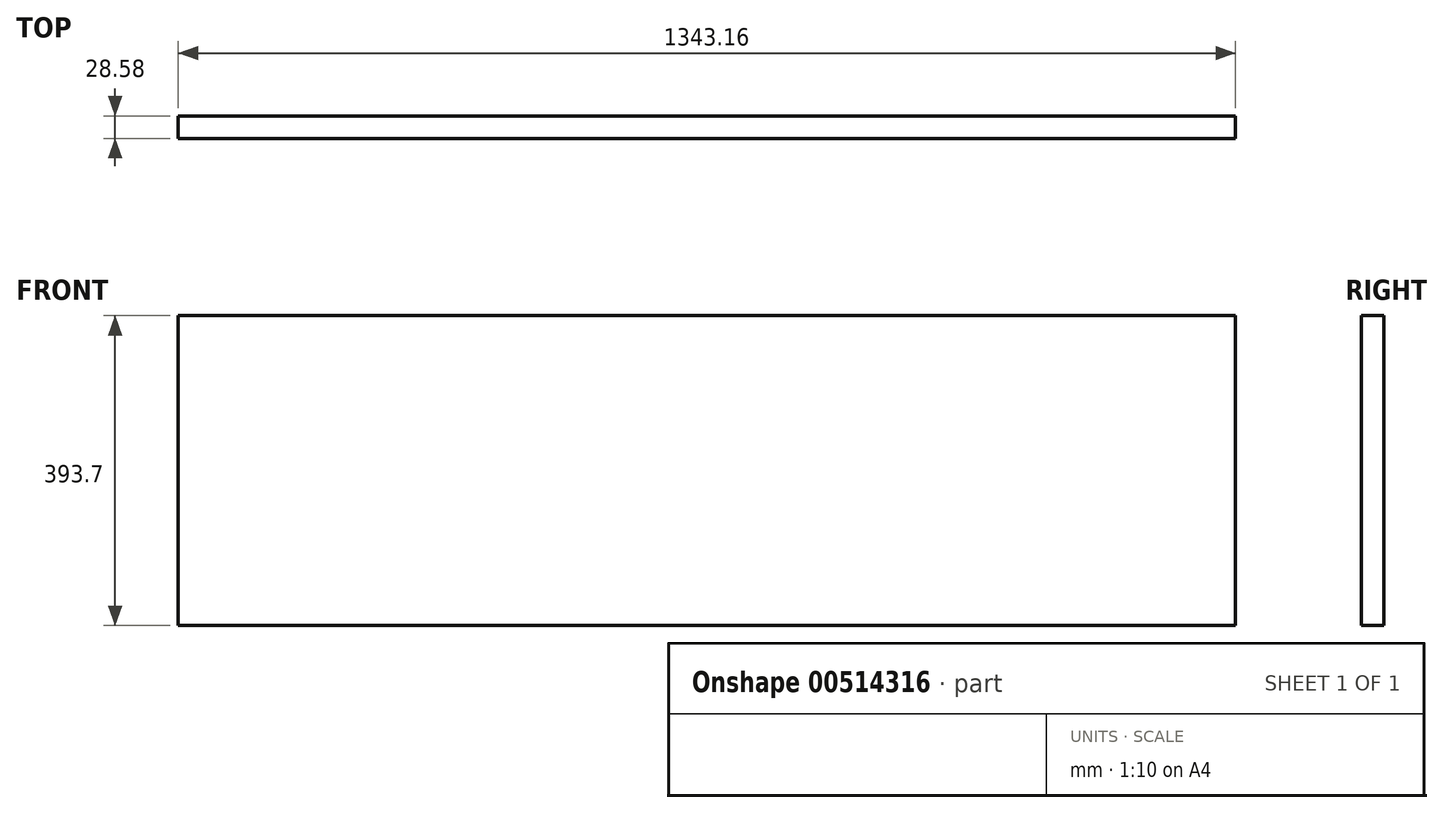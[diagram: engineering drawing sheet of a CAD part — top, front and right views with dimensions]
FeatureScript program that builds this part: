
annotation { "Feature Type Name" : "Feature", "Feature Type Description" : "" }
export const myFeature = defineFeature(function(context is Context, id is Id, definition is map)
    precondition{}
    {
        {
            var Q0;
            Q0=qCreatedBy(makeId("Top.planeOp"),FACE);
            var sketch = newSketch(context, id + "F0", { "sketchPlane" : qUnion([Q0])});
            skLineSegment(sketch, "E0.bottom", {"start": v(671.58, 14.29) * mm, "end": v(-671.58, 14.29) * mm});
            skLineSegment(sketch, "E0.top", {"start": v(671.58, -14.29) * mm, "end": v(-671.58, -14.29) * mm});
            skLineSegment(sketch, "E0.left", {"start": v(671.58, 14.29) * mm, "end": v(671.58, -14.29) * mm});
            skLineSegment(sketch, "E0.right", {"start": v(-671.58, 14.29) * mm, "end": v(-671.58, -14.29) * mm});
            skPoint(sketch, "E0.middle", {"position": v(0, 0) * mm});
            skSolve(sketch);
        }
        {
            var Q0;
            Q0=makeQuery(id+"F0.imprint","IMPRINT",FACE,{"disambiguationData":[TD([[makeQuery(id+"F0.imprint","IMPRINT",EDGE,{"derivedFrom":sQuery(id+"F0.wireOp",EDGE,"E0.bottom")}),1.0]])]});
            extrude(context, id + "F1", {"entities" : qUnion([Q0]), "depth" : 393.7 * mm});
        }
    });
